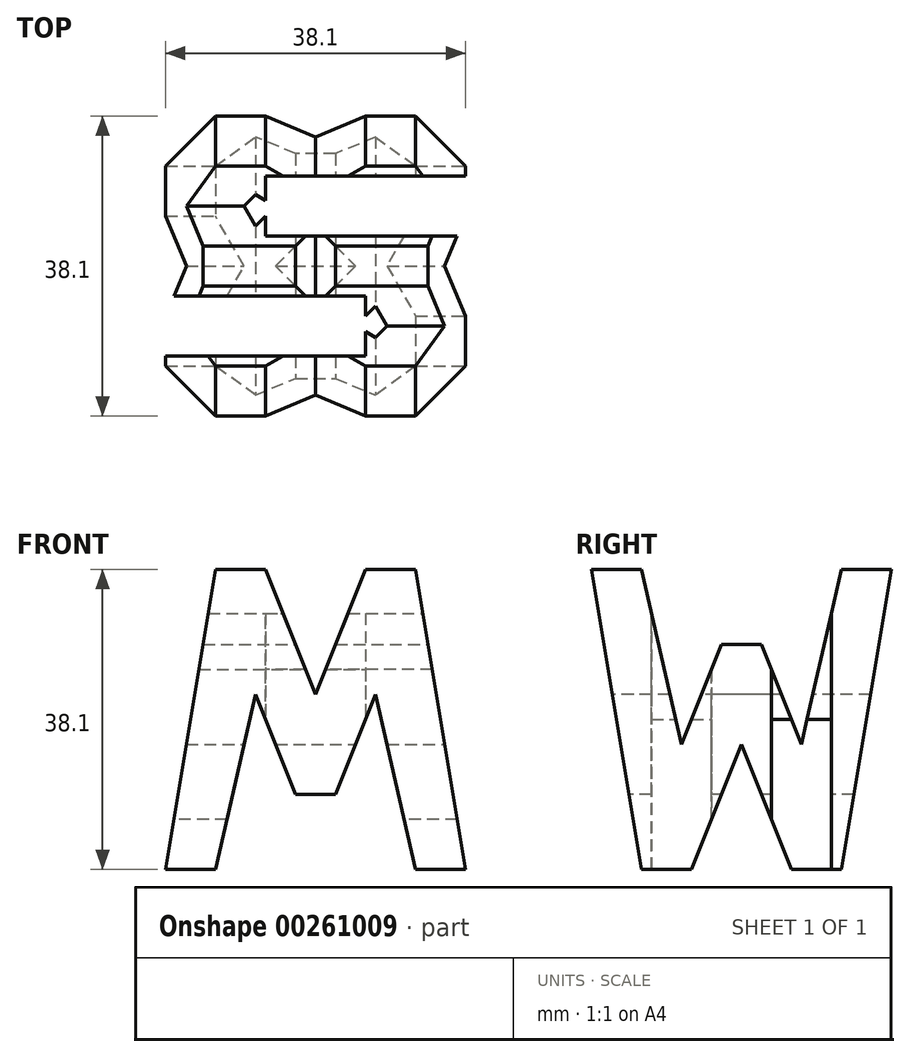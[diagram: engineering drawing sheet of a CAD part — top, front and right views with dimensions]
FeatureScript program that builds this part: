
annotation { "Feature Type Name" : "Feature", "Feature Type Description" : "" }
export const myFeature = defineFeature(function(context is Context, id is Id, definition is map)
    precondition{}
    {
        {
            var Q0;
            Q0=qCreatedBy(makeId("Front.planeOp"),FACE);
            var sketch = newSketch(context, id + "F0", { "sketchPlane" : qUnion([Q0])});
            skLineSegment(sketch, "E0.bottom", {"start": v(38.1, 0) * mm, "end": v(0, 0) * mm});
            skLineSegment(sketch, "E0.top", {"start": v(38.1, 38.1) * mm, "end": v(0, 38.1) * mm});
            skLineSegment(sketch, "E0.left", {"start": v(0, 0) * mm, "end": v(0, 38.1) * mm});
            skLineSegment(sketch, "E0.right", {"start": v(38.1, 0) * mm, "end": v(38.1, 38.1) * mm});
            skSolve(sketch);
        }
        {
            var Q0;
            Q0 = qSketchRegion(id + "F0", true);
            extrude(context, id + "F1", {"entities" : qUnion([Q0]), "depth" : 38.1 * mm});
        }
        {
            var Q0;
            Q0=qCreatedBy(makeId("Front.planeOp"),FACE);
            cPlane(context, id + "F2", {"entities" : qUnion([Q0]), "cplaneType" : CPlaneType.OFFSET, "offset" : 38.1 * mm, "width" : 152.4 * mm, "height" : 152.4 * mm});
        }
        {
            var Q0;
            Q0=qCreatedBy(makeId("Right.planeOp"),FACE);
            cPlane(context, id + "F3", {"entities" : qUnion([Q0]), "cplaneType" : CPlaneType.OFFSET, "offset" : 38.1 * mm, "width" : 152.4 * mm, "height" : 152.4 * mm});
        }
        {
            var Q0;
            Q0=qCreatedBy(makeId("Top.planeOp"),FACE);
            cPlane(context, id + "F4", {"entities" : qUnion([Q0]), "cplaneType" : CPlaneType.OFFSET, "offset" : 38.1 * mm, "width" : 152.4 * mm, "height" : 152.4 * mm});
        }
        {
            var Q0;
            Q0=qCreatedBy(id+"F3.planeOp",FACE);
            var sketch = newSketch(context, id + "F5", { "sketchPlane" : qUnion([Q0])});
            skLineSegment(sketch, "E1.bottom", {"start": v(-38.1, 38.1) * mm, "end": v(0, 38.1) * mm});
            skLineSegment(sketch, "E1.top", {"start": v(-38.1, 0) * mm, "end": v(0, 0) * mm});
            skLineSegment(sketch, "E1.left", {"start": v(-38.1, 38.1) * mm, "end": v(-38.1, 0) * mm});
            skLineSegment(sketch, "E1.right", {"start": v(0, 38.1) * mm, "end": v(0, 0) * mm});
            skLineSegment(sketch, "E2", {"start": v(-38.1, 38.1) * mm, "end": v(-31.75, 0) * mm});
            skLineSegment(sketch, "E3", {"start": v(-6.35, 0) * mm, "end": v(0, 38.1) * mm});
            skLineSegment(sketch, "E4", {"start": v(-31.75, 38.1) * mm, "end": v(-26.67, 15.87) * mm});
            skLineSegment(sketch, "E5", {"start": v(-21.59, 38.1) * mm, "end": v(-16.5, 38.1) * mm});
            skLineSegment(sketch, "E6", {"start": v(-11.43, 15.87) * mm, "end": v(-6.35, 38.1) * mm});
            skLineSegment(sketch, "E7", {"start": v(-25.4, 0) * mm, "end": v(-19.05, 15.88) * mm});
            skLineSegment(sketch, "E8", {"start": v(-19.05, 15.88) * mm, "end": v(-12.7, 0) * mm});
            skLineSegment(sketch, "E9", {"start": v(-21.59, 28.58) * mm, "end": v(-16.51, 28.58) * mm});
            skLineSegment(sketch, "E10", {"start": v(-21.59, 28.58) * mm, "end": v(-26.67, 15.87) * mm});
            skLineSegment(sketch, "E11", {"start": v(-16.51, 28.58) * mm, "end": v(-11.43, 15.87) * mm});
            skSolve(sketch);
        }
        {
            var Q0;
            {var subQ1=sQuery(id+"F5.wireOp",EDGE,"E4");Q0=makeQuery(id+"F5.imprint","IMPRINT",FACE,{"disambiguationData":[TD([[makeQuery(id+"F5.imprint","IMPRINT",EDGE,{"derivedFrom":subQ1}),1.0]])]});}
            var Q1;
            {var subQ0=sQuery(id+"F5.wireOp",EDGE,"E1.left");Q1=makeQuery(id+"F5.imprint","IMPRINT",FACE,{"disambiguationData":[TD([[makeQuery(id+"F5.imprint","IMPRINT",EDGE,{"derivedFrom":subQ0}),1.0]])]});}
            var Q2;
            {var subQ0=sQuery(id+"F5.wireOp",EDGE,"E7");Q2=makeQuery(id+"F5.imprint","IMPRINT",FACE,{"disambiguationData":[TD([[makeQuery(id+"F5.imprint","IMPRINT",EDGE,{"derivedFrom":subQ0}),-1.0]])]});}
            var Q3;
            {var subQ0=sQuery(id+"F5.wireOp",EDGE,"E1.right");Q3=makeQuery(id+"F5.imprint","IMPRINT",FACE,{"disambiguationData":[TD([[makeQuery(id+"F5.imprint","IMPRINT",EDGE,{"derivedFrom":subQ0}),-1.0]])]});}
            extrude(context, id + "F6", {"entities" : qUnion([Q0, Q1, Q2, Q3]), "operationType" : NewBodyOperationType.REMOVE, "oppositeDirection" : true, "depth" : 38.1 * mm});
        }
        {
            var Q0;
            Q0=qCreatedBy(id+"F2.planeOp",FACE);
            var sketch = newSketch(context, id + "F7", { "sketchPlane" : qUnion([Q0])});
            skLineSegment(sketch, "E12", {"start": v(0, 38.1) * mm, "end": v(0, 0) * mm});
            skLineSegment(sketch, "E13", {"start": v(0, 0) * mm, "end": v(38.1, 0) * mm});
            skLineSegment(sketch, "E14", {"start": v(38.1, 0) * mm, "end": v(38.1, 38.1) * mm});
            skLineSegment(sketch, "E15", {"start": v(38.1, 38.1) * mm, "end": v(0, 38.1) * mm});
            skLineSegment(sketch, "E16", {"start": v(0, 0) * mm, "end": v(6.35, 38.1) * mm});
            skLineSegment(sketch, "E17", {"start": v(12.7, 38.1) * mm, "end": v(19.05, 22.22) * mm});
            skLineSegment(sketch, "E18", {"start": v(19.05, 22.23) * mm, "end": v(25.4, 38.1) * mm});
            skLineSegment(sketch, "E19", {"start": v(31.75, 38.1) * mm, "end": v(38.1, 0) * mm});
            skLineSegment(sketch, "E20", {"start": v(31.75, 0) * mm, "end": v(26.67, 22.23) * mm});
            skLineSegment(sketch, "E21", {"start": v(11.43, 22.23) * mm, "end": v(6.35, 0) * mm});
            skLineSegment(sketch, "E22", {"start": v(11.43, 22.23) * mm, "end": v(16.51, 9.52) * mm});
            skLineSegment(sketch, "E23", {"start": v(16.51, 9.53) * mm, "end": v(21.59, 9.53) * mm});
            skLineSegment(sketch, "E24", {"start": v(21.6, 9.53) * mm, "end": v(26.67, 22.23) * mm});
            skSolve(sketch);
        }
        {
            var Q0;
            {var subQ0=sQuery(id+"F7.wireOp",EDGE,"E12");Q0=makeQuery(id+"F7.imprint","IMPRINT",FACE,{"disambiguationData":[TD([[makeQuery(id+"F7.imprint","IMPRINT",EDGE,{"derivedFrom":subQ0}),1.0]])]});}
            var Q1;
            {var subQ0=sQuery(id+"F7.wireOp",EDGE,"E17");Q1=makeQuery(id+"F7.imprint","IMPRINT",FACE,{"disambiguationData":[TD([[makeQuery(id+"F7.imprint","IMPRINT",EDGE,{"derivedFrom":subQ0}),1.0]])]});}
            var Q2;
            {var subQ0=sQuery(id+"F7.wireOp",EDGE,"E20");Q2=makeQuery(id+"F7.imprint","IMPRINT",FACE,{"disambiguationData":[TD([[makeQuery(id+"F7.imprint","IMPRINT",EDGE,{"derivedFrom":subQ0}),1.0]])]});}
            var Q3;
            {var subQ0=sQuery(id+"F7.wireOp",EDGE,"E14");Q3=makeQuery(id+"F7.imprint","IMPRINT",FACE,{"disambiguationData":[TD([[makeQuery(id+"F7.imprint","IMPRINT",EDGE,{"derivedFrom":subQ0}),1.0]])]});}
            extrude(context, id + "F8", {"entities" : qUnion([Q0, Q1, Q2, Q3]), "operationType" : NewBodyOperationType.REMOVE, "oppositeDirection" : true, "depth" : 38.1 * mm});
        }
        {
            var Q0;
            Q0=qCreatedBy(id+"F4.planeOp",FACE);
            var sketch = newSketch(context, id + "F9", { "sketchPlane" : qUnion([Q0])});
            skLineSegment(sketch, "E25", {"start": v(0, 0) * mm, "end": v(38.1, 0) * mm});
            skLineSegment(sketch, "E26", {"start": v(38.1, 0) * mm, "end": v(38.1, -38.1) * mm});
            skLineSegment(sketch, "E27", {"start": v(38.1, -38.1) * mm, "end": v(0, -38.1) * mm});
            skLineSegment(sketch, "E28", {"start": v(0, -38.1) * mm, "end": v(0, 0) * mm});
            skLineSegment(sketch, "E29", {"start": v(12.7, -15.24) * mm, "end": v(38.1, -15.24) * mm});
            skLineSegment(sketch, "E30", {"start": v(38.1, -15.24) * mm, "end": v(38.1, -7.62) * mm});
            skLineSegment(sketch, "E31", {"start": v(0, -22.86) * mm, "end": v(25.4, -22.86) * mm});
            skPoint(sketch, "E31.endSnap0", {"position": v(25.4, -15.24) * mm});
            skLineSegment(sketch, "E32", {"start": v(25.4, -22.86) * mm, "end": v(25.4, -30.48) * mm});
            skLineSegment(sketch, "E33", {"start": v(25.4, -30.48) * mm, "end": v(0, -30.48) * mm});
            skLineSegment(sketch, "E34", {"start": v(0, -30.48) * mm, "end": v(0, -22.86) * mm});
            skLineSegment(sketch, "E35", {"start": v(38.1, -7.62) * mm, "end": v(12.7, -7.62) * mm});
            skLineSegment(sketch, "E36", {"start": v(12.7, -15.24) * mm, "end": v(12.7, -7.62) * mm});
            skSolve(sketch);
        }
        {
            var Q0;
            Q0=makeQuery(id+"F9.imprint","IMPRINT",FACE,{"disambiguationData":[TD([[makeQuery(id+"F9.imprint","IMPRINT",EDGE,{"derivedFrom":sQuery(id+"F9.wireOp",EDGE,"E29")}),1.0]])]});
            var Q1;
            Q1=makeQuery(id+"F9.imprint","IMPRINT",FACE,{"disambiguationData":[TD([[makeQuery(id+"F9.imprint","IMPRINT",EDGE,{"derivedFrom":sQuery(id+"F9.wireOp",EDGE,"E31")}),-1.0]])]});
            extrude(context, id + "F10", {"entities" : qUnion([Q0, Q1]), "operationType" : NewBodyOperationType.REMOVE, "oppositeDirection" : true, "depth" : 38.1 * mm});
        }
    });
